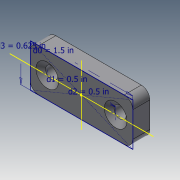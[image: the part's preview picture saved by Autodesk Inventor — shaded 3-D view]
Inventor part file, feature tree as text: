
AUTODESK INVENTOR PART (.ipt)
format: ipt  version: 2018.3 (Build 223284000, 284)  size: 119,296 bytes
history: native  units: in
note: dims shown in document units (in); Inventor stores cm internally (conversion verified against a paired STEP export)
features: sketch x1, extrude x1, hole x1, fillet x1
ambient origin geometry x8: Origin, YZ Plane, XZ Plane, XY Plane, X Axis, Y Axis, Z Axis, Center Point
bodies: Solid1 (feature_tree)
feature tree (4):
  sketch  "Sketch1"  dims[d0=1.5in d1=0.5in d2=0.5in d3=0.625in d4=0.25in d5=0.0in d6=0.177in d7=0.75in d8=0.332in d9=0.25in d10=0.6871in d11=1.0in d12=0.8108in d13=0.125in]
  extrude  "Extrusion1"  Depth=0.125in
  hole  "Hole1"  [1 undecoded]
  fillet  "Fillet1"  Radius=0.625in
note: 1 required parameter value undecoded (feature->parameter linkage not recoverable at this tier; creation-order binding heuristic only, values carry confidence <= 0.55)
